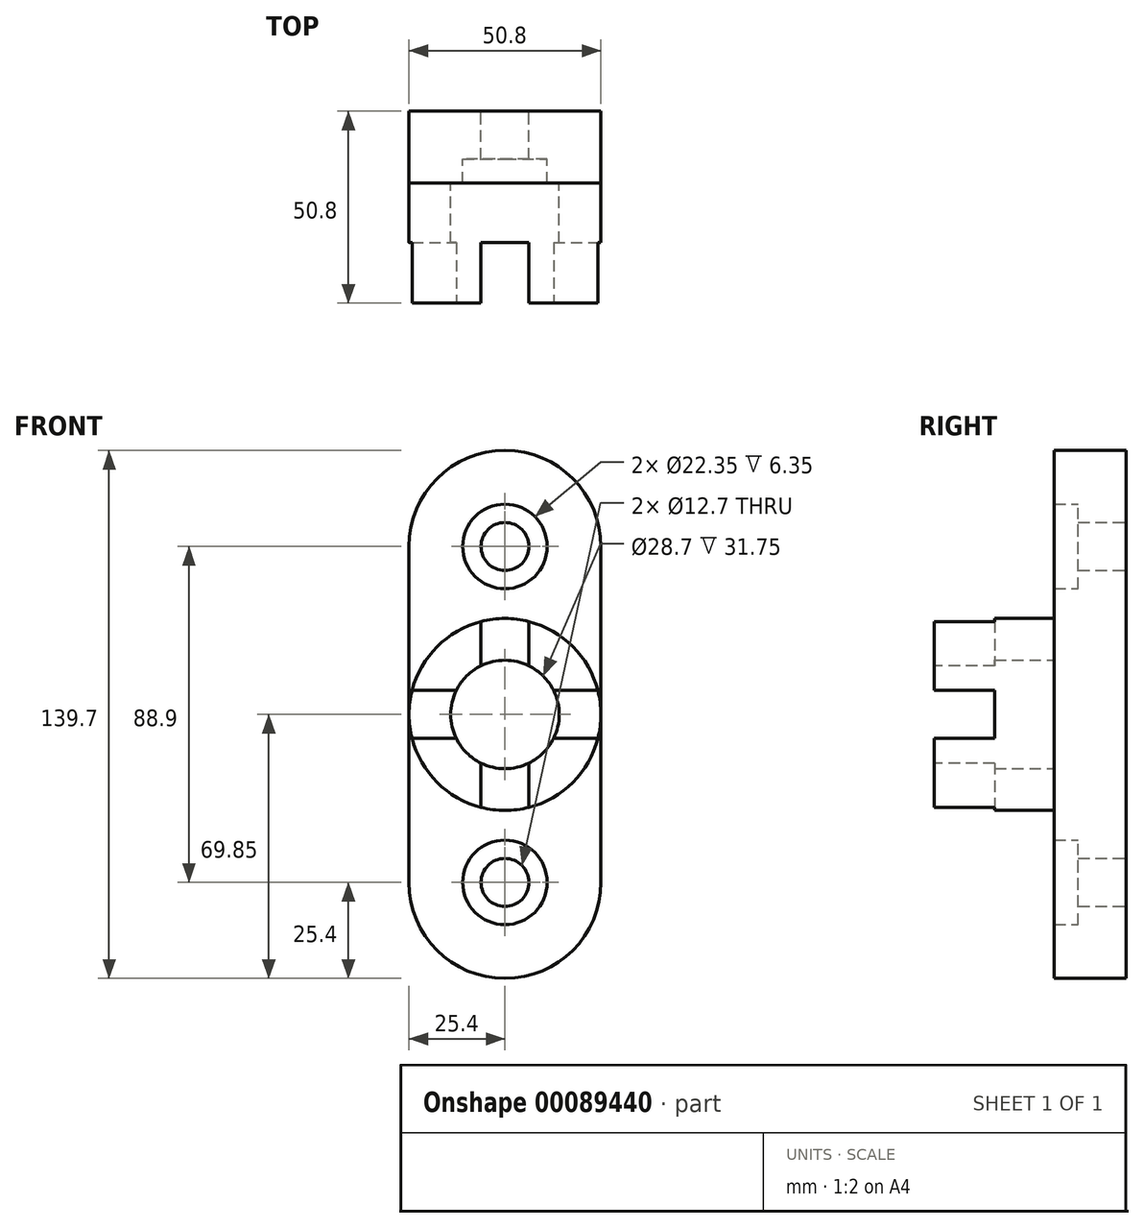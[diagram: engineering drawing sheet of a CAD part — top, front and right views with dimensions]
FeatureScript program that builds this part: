
annotation { "Feature Type Name" : "Feature", "Feature Type Description" : "" }
export const myFeature = defineFeature(function(context is Context, id is Id, definition is map)
    precondition{}
    {
        {
            var Q0;
            Q0=qCreatedBy(makeId("Front.planeOp"),FACE);
            var sketch = newSketch(context, id + "F0", { "sketchPlane" : qUnion([Q0])});
            skLineSegment(sketch, "E0", {"start": v(0, 0) * mm, "end": v(0, -44.45) * mm, "construction": true});
            skLineSegment(sketch, "E1", {"start": v(0, 0) * mm, "end": v(0, 44.45) * mm, "construction": true});
            skCircle(sketch, "E2", {"center": v(0, -44.45) * mm, "radius": 6.35 * mm});
            skCircle(sketch, "E3", {"center": v(0, -44.45) * mm, "radius": 11.18 * mm});
            skCircle(sketch, "E4", {"center": v(0, 44.45) * mm, "radius": 6.35 * mm});
            skCircle(sketch, "E5", {"center": v(0, 44.45) * mm, "radius": 11.18 * mm});
            skArc(sketch, "E6", {"start": v(0, -69.85) * mm, "mid": v(-17.96, -62.41) * mm, "end": v(-25.4, -44.45) * mm});
            skArc(sketch, "E7", {"start": v(0, -69.85) * mm, "mid": v(17.96, -62.41) * mm, "end": v(25.4, -44.45) * mm});
            skArc(sketch, "E8", {"start": v(0, 69.85) * mm, "mid": v(-17.96, 62.41) * mm, "end": v(-25.4, 44.45) * mm});
            skArc(sketch, "E9", {"start": v(0, 69.85) * mm, "mid": v(17.96, 62.41) * mm, "end": v(25.4, 44.45) * mm});
            skLineSegment(sketch, "E10", {"start": v(-25.4, 44.45) * mm, "end": v(-25.4, -44.45) * mm});
            skLineSegment(sketch, "E11", {"start": v(25.4, 44.45) * mm, "end": v(25.4, -44.45) * mm});
            skSolve(sketch);
        }
        {
            var Q0;
            Q0=makeQuery(id+"F0.imprint","IMPRINT",FACE,{"disambiguationData":[TD([[makeQuery(id+"F0.imprint","IMPRINT",EDGE,{"derivedFrom":sQuery(id+"F0.wireOp",EDGE,"E3")}),-1.0]])]});
            extrude(context, id + "F1", {"entities" : qUnion([Q0]), "depth" : 19.05 * mm});
        }
        {
            var Q0;
            Q0=makeQuery(id+"F0.imprint","IMPRINT",FACE,{"disambiguationData":[TD([[makeQuery(id+"F0.imprint","IMPRINT",EDGE,{"derivedFrom":sQuery(id+"F0.wireOp",EDGE,"E2")}),-1.0]])]});
            var Q1;
            Q1=makeQuery(id+"F0.imprint","IMPRINT",FACE,{"disambiguationData":[TD([[makeQuery(id+"F0.imprint","IMPRINT",EDGE,{"derivedFrom":sQuery(id+"F0.wireOp",EDGE,"E4")}),-1.0]])]});
            extrude(context, id + "F2", {"entities" : qUnion([Q0, Q1]), "operationType" : NewBodyOperationType.ADD, "depth" : 12.7 * mm});
        }
        {
            var Q0;
            Q0=makeQuery(id+"F1.opExtrude","CAP_FACE",FACE,{"disambiguationData":[OSD([sQuery(id+"F0.wireOp",EDGE,"E3"),sQuery(id+"F0.wireOp",EDGE,"E5"),sQuery(id+"F0.wireOp",EDGE,"E6"),sQuery(id+"F0.wireOp",EDGE,"E7"),sQuery(id+"F0.wireOp",EDGE,"E8"),sQuery(id+"F0.wireOp",EDGE,"E9"),sQuery(id+"F0.wireOp",EDGE,"E10"),sQuery(id+"F0.wireOp",EDGE,"E11")])],"isStart":false});
            var sketch = newSketch(context, id + "F3", { "sketchPlane" : qUnion([Q0])});
            skCircle(sketch, "E12", {"center": v(0, 0) * mm, "radius": 14.35 * mm});
            skLineSegment(sketch, "E13", {"start": v(-25.4, 0) * mm, "end": v(25.4, 0) * mm, "construction": true});
            skLineSegment(sketch, "E14", {"start": v(-24.6, -6.35) * mm, "end": v(24.6, -6.35) * mm, "construction": true});
            skLineSegment(sketch, "E15", {"start": v(0, 25.4) * mm, "end": v(0, -25.4) * mm, "construction": true});
            skPoint(sketch, "E15.startSnap0", {"position": v(0, 4.2) * mm});
            skPoint(sketch, "E15.endSnap0", {"position": v(0, -6.35) * mm});
            skLineSegment(sketch, "E16", {"start": v(-25.4, 25.4) * mm, "end": v(25.4, 25.4) * mm, "construction": true});
            skLineSegment(sketch, "E17", {"start": v(-25.4, -25.4) * mm, "end": v(25.4, -25.4) * mm, "construction": true});
            skLineSegment(sketch, "E18", {"start": v(-24.6, 6.35) * mm, "end": v(24.6, 6.35) * mm, "construction": true});
            skLineSegment(sketch, "E19", {"start": v(-6.35, 24.6) * mm, "end": v(-6.35, -24.6) * mm, "construction": true});
            skLineSegment(sketch, "E20", {"start": v(6.35, 24.6) * mm, "end": v(6.35, -24.6) * mm, "construction": true});
            skArc(sketch, "E21", {"start": v(-24.58, 6.4) * mm, "mid": v(-25.4, 0.02) * mm, "end": v(-24.6, -6.35) * mm});
            skArc(sketch, "E22", {"start": v(-24.6, -6.35) * mm, "mid": v(-17.96, -17.96) * mm, "end": v(-6.35, -24.6) * mm});
            skArc(sketch, "E23", {"start": v(24.6, 6.35) * mm, "mid": v(17.96, 17.96) * mm, "end": v(6.35, 24.6) * mm});
            skArc(sketch, "E24", {"start": v(24.67, -6.05) * mm, "mid": v(25.4, 0.15) * mm, "end": v(24.6, 6.35) * mm});
            skArc(sketch, "E25", {"start": v(-6.35, -24.6) * mm, "mid": v(0, -25.4) * mm, "end": v(6.35, -24.6) * mm});
            skArc(sketch, "E26", {"start": v(6.35, -24.6) * mm, "mid": v(18.07, -17.85) * mm, "end": v(24.67, -6.05) * mm});
            skArc(sketch, "E27", {"start": v(6.35, 24.6) * mm, "mid": v(0, 25.4) * mm, "end": v(-6.35, 24.6) * mm});
            skArc(sketch, "E28", {"start": v(-6.35, 24.6) * mm, "mid": v(-17.94, 17.98) * mm, "end": v(-24.58, 6.4) * mm});
            skLineSegment(sketch, "E29", {"start": v(-6.35, -12.87) * mm, "end": v(-6.35, -24.6) * mm});
            skLineSegment(sketch, "E30", {"start": v(6.35, -12.87) * mm, "end": v(6.35, -24.6) * mm});
            skLineSegment(sketch, "E31", {"start": v(12.87, -6.35) * mm, "end": v(24.6, -6.35) * mm});
            skLineSegment(sketch, "E32", {"start": v(12.87, 6.35) * mm, "end": v(24.6, 6.35) * mm});
            skLineSegment(sketch, "E33", {"start": v(-24.6, 6.35) * mm, "end": v(-12.87, 6.35) * mm});
            skLineSegment(sketch, "E34", {"start": v(-24.6, -6.35) * mm, "end": v(-12.87, -6.35) * mm});
            skLineSegment(sketch, "E35", {"start": v(-6.35, 24.6) * mm, "end": v(-6.35, 12.87) * mm});
            skLineSegment(sketch, "E36", {"start": v(6.35, 24.6) * mm, "end": v(6.35, 12.87) * mm});
            skSolve(sketch);
        }
        {
            var Q0;
            Q0=qSketchRegion(id+"F3",true);
            extrude(context, id + "F4", {"entities" : qUnion([Q0]), "operationType" : NewBodyOperationType.ADD, "depth" : 31.75 * mm});
        }
        {
            var Q0;
            Q0=makeQuery(id+"F4.opExtrude","CAP_FACE",FACE,{"disambiguationData":[OSD([sQuery(id+"F3.wireOp",EDGE,"E12"),sQuery(id+"F3.wireOp",EDGE,"E21"),sQuery(id+"F3.wireOp",EDGE,"E22"),sQuery(id+"F3.wireOp",EDGE,"E23"),sQuery(id+"F3.wireOp",EDGE,"E24"),sQuery(id+"F3.wireOp",EDGE,"E25"),sQuery(id+"F3.wireOp",EDGE,"E26"),sQuery(id+"F3.wireOp",EDGE,"E27"),sQuery(id+"F3.wireOp",EDGE,"E28")])],"isStart":false});
            var sketch = newSketch(context, id + "F5", { "sketchPlane" : qUnion([Q0])});
            skLineSegment(sketch, "E37.0", {"start": v(-6.35, 24.6) * mm, "end": v(-6.35, 12.87) * mm});
            skLineSegment(sketch, "E38.0", {"start": v(6.35, 24.6) * mm, "end": v(6.35, 12.87) * mm});
            skArc(sketch, "E39.0", {"start": v(6.35, 24.6) * mm, "mid": v(0, 25.4) * mm, "end": v(-6.35, 24.6) * mm});
            skArc(sketch, "E40.0", {"start": v(-24.58, 6.4) * mm, "mid": v(-25.4, 0.02) * mm, "end": v(-24.6, -6.35) * mm});
            skLineSegment(sketch, "E41.0", {"start": v(-24.6, 6.35) * mm, "end": v(-12.87, 6.35) * mm});
            skLineSegment(sketch, "E42.0", {"start": v(-24.6, -6.35) * mm, "end": v(-12.87, -6.35) * mm});
            skLineSegment(sketch, "E43.0", {"start": v(6.35, -12.87) * mm, "end": v(6.35, -24.6) * mm});
            skLineSegment(sketch, "E44.0", {"start": v(-6.35, -12.87) * mm, "end": v(-6.35, -24.6) * mm});
            skArc(sketch, "E45.0", {"start": v(-6.35, -24.6) * mm, "mid": v(0, -25.4) * mm, "end": v(6.35, -24.6) * mm});
            skLineSegment(sketch, "E46.0", {"start": v(12.87, -6.35) * mm, "end": v(24.6, -6.35) * mm});
            skLineSegment(sketch, "E47.0", {"start": v(12.87, 6.35) * mm, "end": v(24.6, 6.35) * mm});
            skArc(sketch, "E48.0", {"start": v(24.67, -6.05) * mm, "mid": v(25.4, 0.15) * mm, "end": v(24.6, 6.35) * mm});
            skSolve(sketch);
        }
        {
            var Q0;
            {var subQ0=sQuery(id+"F5.wireOp",EDGE,"E46.0");Q0=makeQuery(id+"F5.imprint","IMPRINT",FACE,{"disambiguationData":[TD([[makeQuery(id+"F5.imprint","IMPRINT",EDGE,{"derivedFrom":subQ0}),1.0]])]});}
            var Q1;
            {var subQ2=sQuery(id+"F5.wireOp",EDGE,"E41.0");Q1=makeQuery(id+"F5.imprint","IMPRINT",FACE,{"disambiguationData":[TD([[makeQuery(id+"F5.imprint","IMPRINT",EDGE,{"derivedFrom":subQ2}),-1.0]])]});}
            var Q2;
            {var subQ0=sQuery(id+"F5.wireOp",EDGE,"E43.0");Q2=makeQuery(id+"F5.imprint","IMPRINT",FACE,{"disambiguationData":[TD([[makeQuery(id+"F5.imprint","IMPRINT",EDGE,{"derivedFrom":subQ0}),-1.0]])]});}
            var Q3;
            {var subQ0=sQuery(id+"F5.wireOp",EDGE,"E37.0");Q3=makeQuery(id+"F5.imprint","IMPRINT",FACE,{"disambiguationData":[TD([[makeQuery(id+"F5.imprint","IMPRINT",EDGE,{"derivedFrom":subQ0}),1.0]])]});}
            extrude(context, id + "F6", {"entities" : qUnion([Q0, Q1, Q2, Q3]), "operationType" : NewBodyOperationType.REMOVE, "oppositeDirection" : true, "depth" : 16 * mm});
        }
    });
